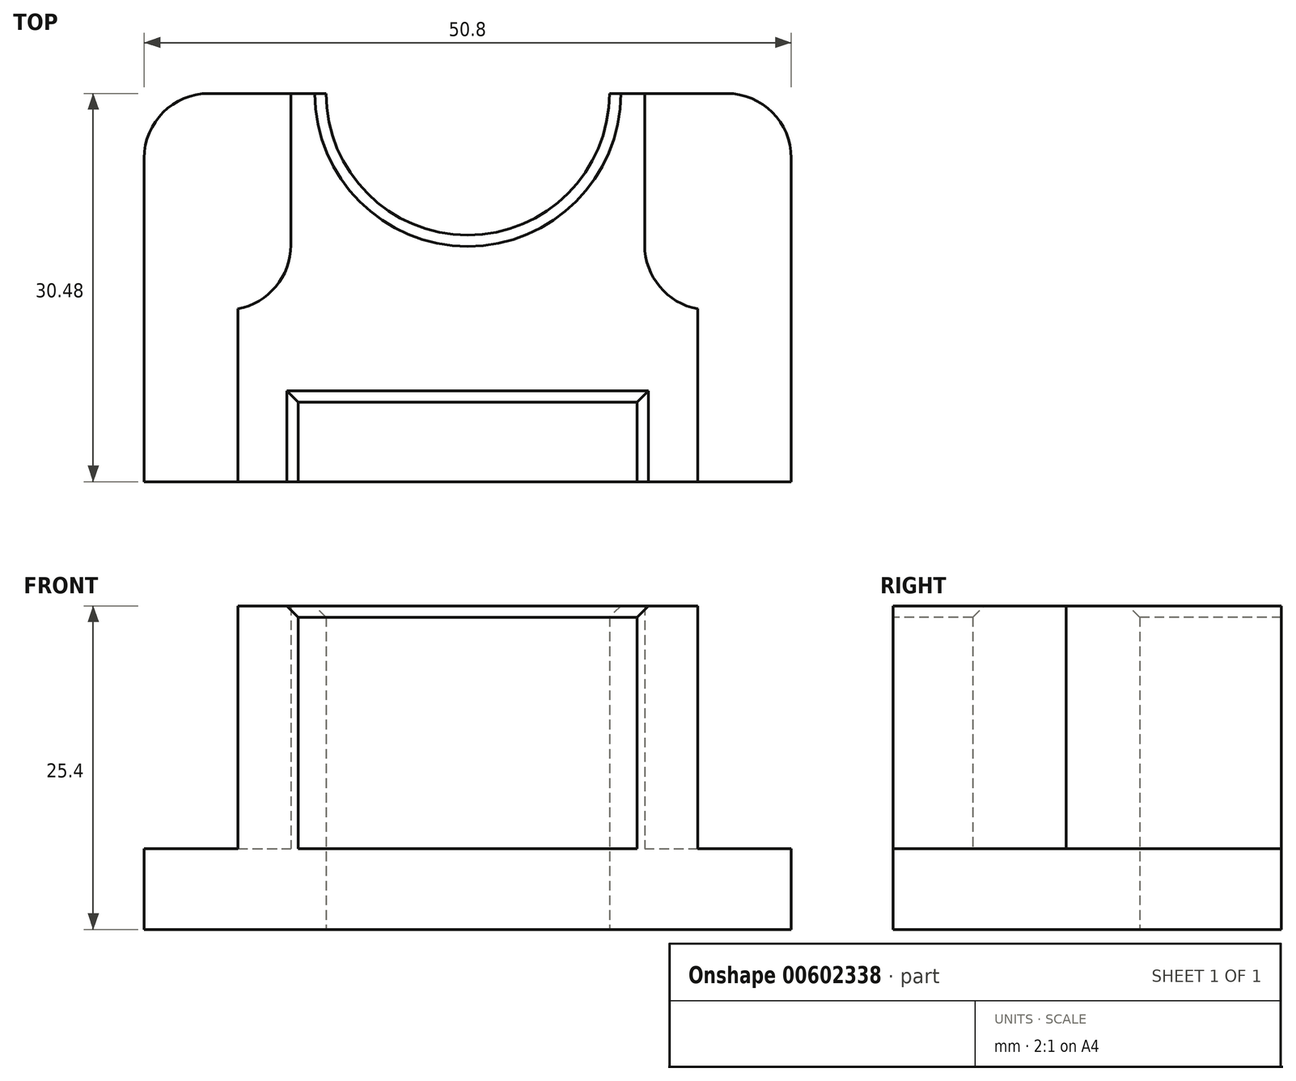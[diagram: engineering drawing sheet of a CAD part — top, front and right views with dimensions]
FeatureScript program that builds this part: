
annotation { "Feature Type Name" : "Feature", "Feature Type Description" : "" }
export const myFeature = defineFeature(function(context is Context, id is Id, definition is map)
    precondition{}
    {
        {
            var Q0;
            Q0=qCreatedBy(makeId("Top.planeOp"),FACE);
            var sketch = newSketch(context, id + "F0", { "sketchPlane" : qUnion([Q0])});
            skLineSegment(sketch, "E0.bottom", {"start": v(0, 0) * mm, "end": v(50.8, 0) * mm});
            skLineSegment(sketch, "E0.top", {"start": v(0, 30.48) * mm, "end": v(50.8, 30.48) * mm});
            skLineSegment(sketch, "E0.left", {"start": v(0, 0) * mm, "end": v(0, 30.48) * mm});
            skLineSegment(sketch, "E0.right", {"start": v(50.8, 0) * mm, "end": v(50.8, 30.48) * mm});
            skPoint(sketch, "E1", {"position": v(25.4, 30.48) * mm});
            skArc(sketch, "E2", {"start": v(14.28, 30.48) * mm, "mid": v(25.4, 19.36) * mm, "end": v(36.52, 30.48) * mm});
            skPoint(sketch, "E3", {"position": v(25.4, 0) * mm});
            skLineSegment(sketch, "E4.bottom", {"start": v(38.7, 6.24) * mm, "end": v(12.1, 6.24) * mm});
            skLineSegment(sketch, "E4.left", {"start": v(38.7, 6.24) * mm, "end": v(38.7, 0) * mm});
            skLineSegment(sketch, "E4.right", {"start": v(12.1, 6.24) * mm, "end": v(12.1, 0) * mm});
            skLineSegment(sketch, "E5", {"start": v(43.45, 0) * mm, "end": v(43.45, 13.57) * mm});
            skLineSegment(sketch, "E6", {"start": v(43.45, 13.57) * mm, "end": v(39.3, 13.57) * mm});
            skLineSegment(sketch, "E7", {"start": v(39.3, 13.57) * mm, "end": v(39.3, 30.48) * mm});
            skLineSegment(sketch, "E8", {"start": v(25.4, 30.48) * mm, "end": v(25.4, 0) * mm, "construction": true});
            skLineSegment(sketch, "E9.MirrorCS", {"start": v(7.35, 0) * mm, "end": v(7.35, 13.57) * mm});
            skLineSegment(sketch, "E10.MirrorCS", {"start": v(11.5, 13.57) * mm, "end": v(11.5, 30.48) * mm});
            skLineSegment(sketch, "E11.MirrorCS", {"start": v(7.35, 13.57) * mm, "end": v(11.5, 13.57) * mm});
            skPoint(sketch, "E4.top.end.orphan", {"position": v(12.1, -6.24) * mm});
            skPoint(sketch, "E12.orphan", {"position": v(38.7, -6.24) * mm});
            skSolve(sketch);
        }
        {
            var Q0;
            {var subQ2=sQuery(id+"F0.wireOp",EDGE,"E2");Q0=makeQuery(id+"F0.imprint","IMPRINT",FACE,{"disambiguationData":[TD([[makeQuery(id+"F0.imprint","IMPRINT",EDGE,{"derivedFrom":subQ2}),-1.0]])]});}
            extrude(context, id + "F1", {"entities" : qUnion([Q0]), "depth" : 19.05 * mm, "offsetDistance" : 25.4 * mm});
        }
        {
            var Q0;
            {var subQ1=sQuery(id+"F0.wireOp",EDGE,"E0.left");Q0=makeQuery(id+"F0.imprint","IMPRINT",FACE,{"disambiguationData":[TD([[makeQuery(id+"F0.imprint","IMPRINT",EDGE,{"derivedFrom":subQ1}),-1.0]])]});}
            var Q1;
            Q1=makeQuery(id+"F0.imprint","IMPRINT",FACE,{"disambiguationData":[TD([[makeQuery(id+"F0.imprint","IMPRINT",EDGE,{"derivedFrom":sQuery(id+"F0.wireOp",EDGE,"E4.bottom")}),1.0]])]});
            var Q2;
            {var subQ1=sQuery(id+"F0.wireOp",EDGE,"E0.right");Q2=makeQuery(id+"F0.imprint","IMPRINT",FACE,{"disambiguationData":[TD([[makeQuery(id+"F0.imprint","IMPRINT",EDGE,{"derivedFrom":subQ1}),1.0]])]});}
            var Q3;
            {var subQ2=sQuery(id+"F0.wireOp",EDGE,"E2");Q3=makeQuery(id+"F0.imprint","IMPRINT",FACE,{"disambiguationData":[TD([[makeQuery(id+"F0.imprint","IMPRINT",EDGE,{"derivedFrom":subQ2}),-1.0]])]});}
            extrude(context, id + "F2", {"entities" : qUnion([Q0, Q1, Q2, Q3]), "operationType" : NewBodyOperationType.ADD, "oppositeDirection" : true, "depth" : 6.35 * mm, "offsetDistance" : 25.4 * mm});
        }
        {
            var Q0;
            Q0=makeQuery(id+"F2.opExtrude","SWEPT_EDGE",EDGE,{"disambiguationData":[OSD([sQuery(id+"F0.wireOp",EDGE,"E0.top"),sQuery(id+"F0.wireOp",EDGE,"E0.left")])]});
            var Q1;
            Q1=makeQuery(id+"F2.opExtrude","SWEPT_EDGE",EDGE,{"disambiguationData":[OSD([sQuery(id+"F0.wireOp",EDGE,"E0.top"),sQuery(id+"F0.wireOp",EDGE,"E0.right")])]});
            var Q2;
            Q2=makeQuery(id+"F1.opExtrude","SWEPT_EDGE",EDGE,{"disambiguationData":[OSD([sQuery(id+"F0.wireOp",EDGE,"E10.MirrorCS"),sQuery(id+"F0.wireOp",EDGE,"E11.MirrorCS")])]});
            var Q3;
            Q3=makeQuery(id+"F1.opExtrude","SWEPT_EDGE",EDGE,{"disambiguationData":[OSD([sQuery(id+"F0.wireOp",EDGE,"E6"),sQuery(id+"F0.wireOp",EDGE,"E7")])]});
            fillet(context, id + "F3", {"entities" : qUnion([Q0, Q1, Q2, Q3]), "radius" : 5.08 * mm, "tangentPropagation" : true, "allowEdgeOverflow" : false});
        }
        {
            var Q0;
            Q0=makeQuery(id+"F1.opExtrude","CAP_EDGE",EDGE,{"disambiguationData":[OSD([sQuery(id+"F0.wireOp",EDGE,"E2")])],"isStart":false});
            var Q1;
            Q1=makeQuery(id+"F1.opExtrude","CAP_EDGE",EDGE,{"disambiguationData":[OSD([sQuery(id+"F0.wireOp",EDGE,"E4.bottom")])],"isStart":false});
            var Q2;
            Q2=makeQuery(id+"F1.opExtrude","CAP_EDGE",EDGE,{"disambiguationData":[OSD([sQuery(id+"F0.wireOp",EDGE,"E4.left")])],"isStart":false});
            var Q3;
            Q3=makeQuery(id+"F1.opExtrude","CAP_EDGE",EDGE,{"disambiguationData":[OSD([sQuery(id+"F0.wireOp",EDGE,"E4.right")])],"isStart":false});
            chamfer(context, id + "F4", {"entities" : qUnion([Q0, Q1, Q2, Q3]), "width" : 0.89 * mm, "tangentPropagation" : true});
        }
    });
